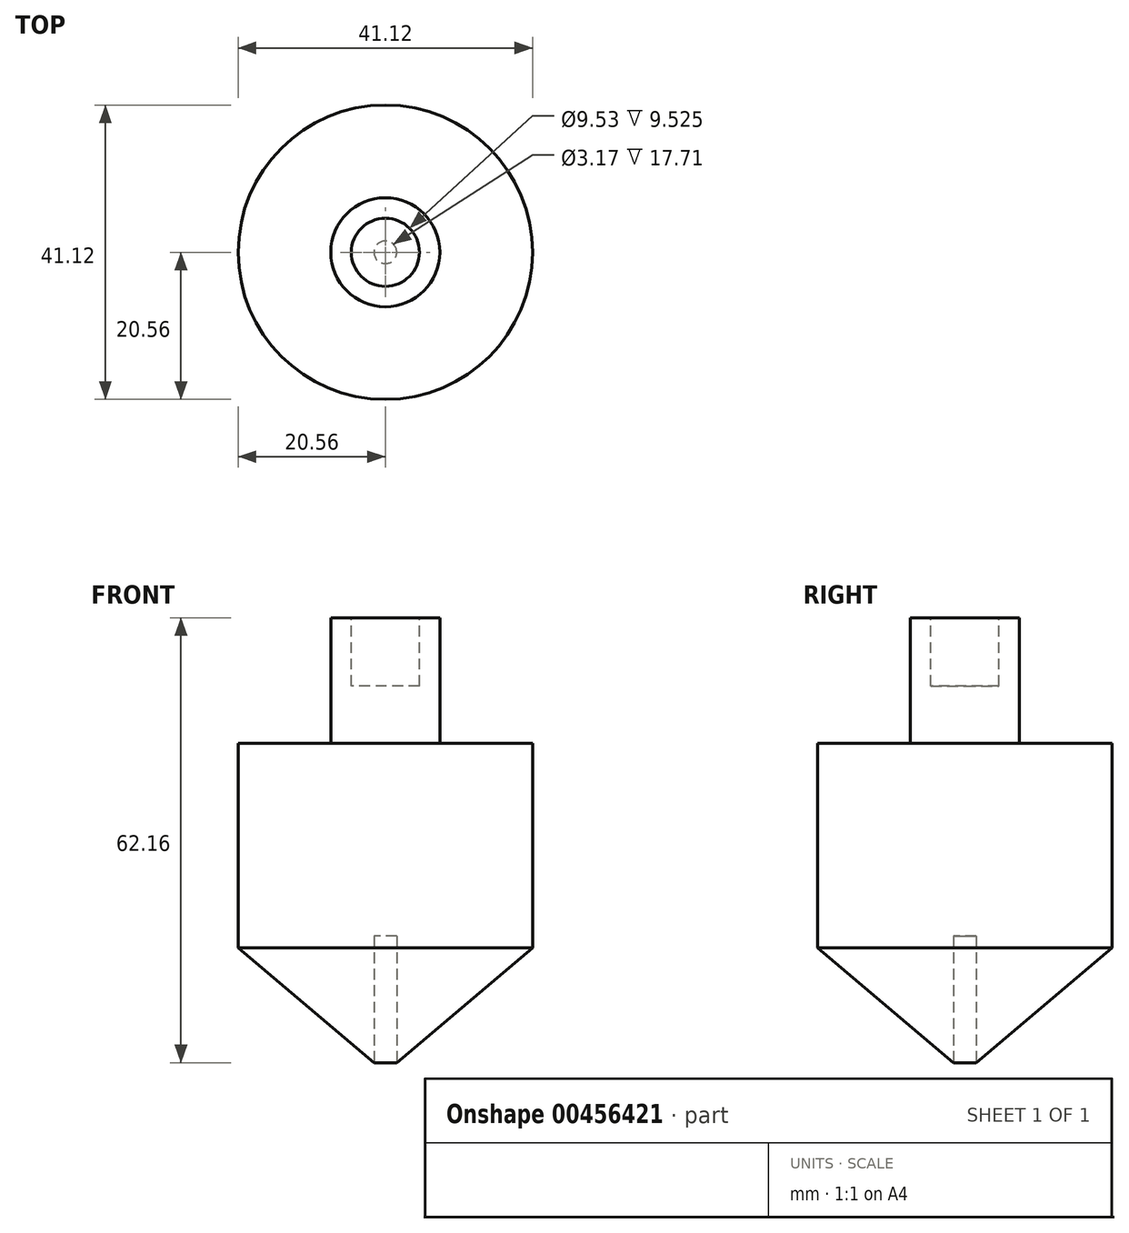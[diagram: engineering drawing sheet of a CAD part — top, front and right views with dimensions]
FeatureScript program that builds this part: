
annotation { "Feature Type Name" : "Feature", "Feature Type Description" : "" }
export const myFeature = defineFeature(function(context is Context, id is Id, definition is map)
    precondition{}
    {
        {
            var Q0;
            Q0=qCreatedBy(makeId("Front.planeOp"),FACE);
            var sketch = newSketch(context, id + "F0", { "sketchPlane" : qUnion([Q0])});
            skLineSegment(sketch, "E0", {"start": v(0, 0) * mm, "end": v(20.56, 17.35) * mm});
            skLineSegment(sketch, "E1", {"start": v(20.56, 17.35) * mm, "end": v(20.56, 55.45) * mm});
            skLineSegment(sketch, "E2", {"start": v(20.56, 55.45) * mm, "end": v(7.62, 55.45) * mm});
            skLineSegment(sketch, "E3", {"start": v(7.62, 55.45) * mm, "end": v(7.62, 63.5) * mm});
            skLineSegment(sketch, "E4", {"start": v(7.62, 63.5) * mm, "end": v(0, 63.5) * mm});
            skLineSegment(sketch, "E5", {"start": v(0, 63.5) * mm, "end": v(0, 0) * mm});
            skSolve(sketch);
        }
        {
            var Q0;
            Q0=makeQuery(id+"F0.imprint","IMPRINT",FACE,{"disambiguationData":[TD([[makeQuery(id+"F0.imprint","IMPRINT",EDGE,{"derivedFrom":sQuery(id+"F0.wireOp",EDGE,"E0")}),1.0]])]});
            var Q1;
            Q1=sQuery(id+"F0.wireOp",EDGE,"E5");
            revolve(context, id + "F1", {"entities" : qUnion([Q0]), "axis" : qUnion([Q1]), "revolveType" : RevolveType.FULL});
        }
        {
            var Q0;
            Q0=makeQuery(id+"F1.opRevolve","SWEPT_FACE",FACE,{"disambiguationData":[OSD([sQuery(id+"F0.wireOp",EDGE,"E4")])]});
            var sketch = newSketch(context, id + "F2", { "sketchPlane" : qUnion([Q0])});
            skCircle(sketch, "E6", {"center": v(0, 0) * mm, "radius": 4.76 * mm});
            skSolve(sketch);
        }
        {
            var Q0;
            Q0=qSketchRegion(id+"F2",true);
            var Q1;
            Q1=makeQuery(id+"F1.opRevolve","SWEPT_FACE",FACE,{"disambiguationData":[OSD([sQuery(id+"F0.wireOp",EDGE,"E2")])]});
            extrude(context, id + "F3", {"entities" : qUnion([Q0, Q1]), "operationType" : NewBodyOperationType.REMOVE, "oppositeDirection" : true, "depth" : 9.52 * mm});
        }
        {
            var Q0;
            Q0=qCreatedBy(makeId("Top.planeOp"),FACE);
            var sketch = newSketch(context, id + "F4", { "sketchPlane" : qUnion([Q0])});
            skCircle(sketch, "E7", {"center": v(0, 0) * mm, "radius": 1.59 * mm});
            skSolve(sketch);
        }
        {
            var Q0;
            Q0=qSketchRegion(id+"F4",true);
            extrude(context, id + "F5", {"entities" : qUnion([Q0]), "operationType" : NewBodyOperationType.REMOVE, "depth" : 19.05 * mm});
        }
    });
